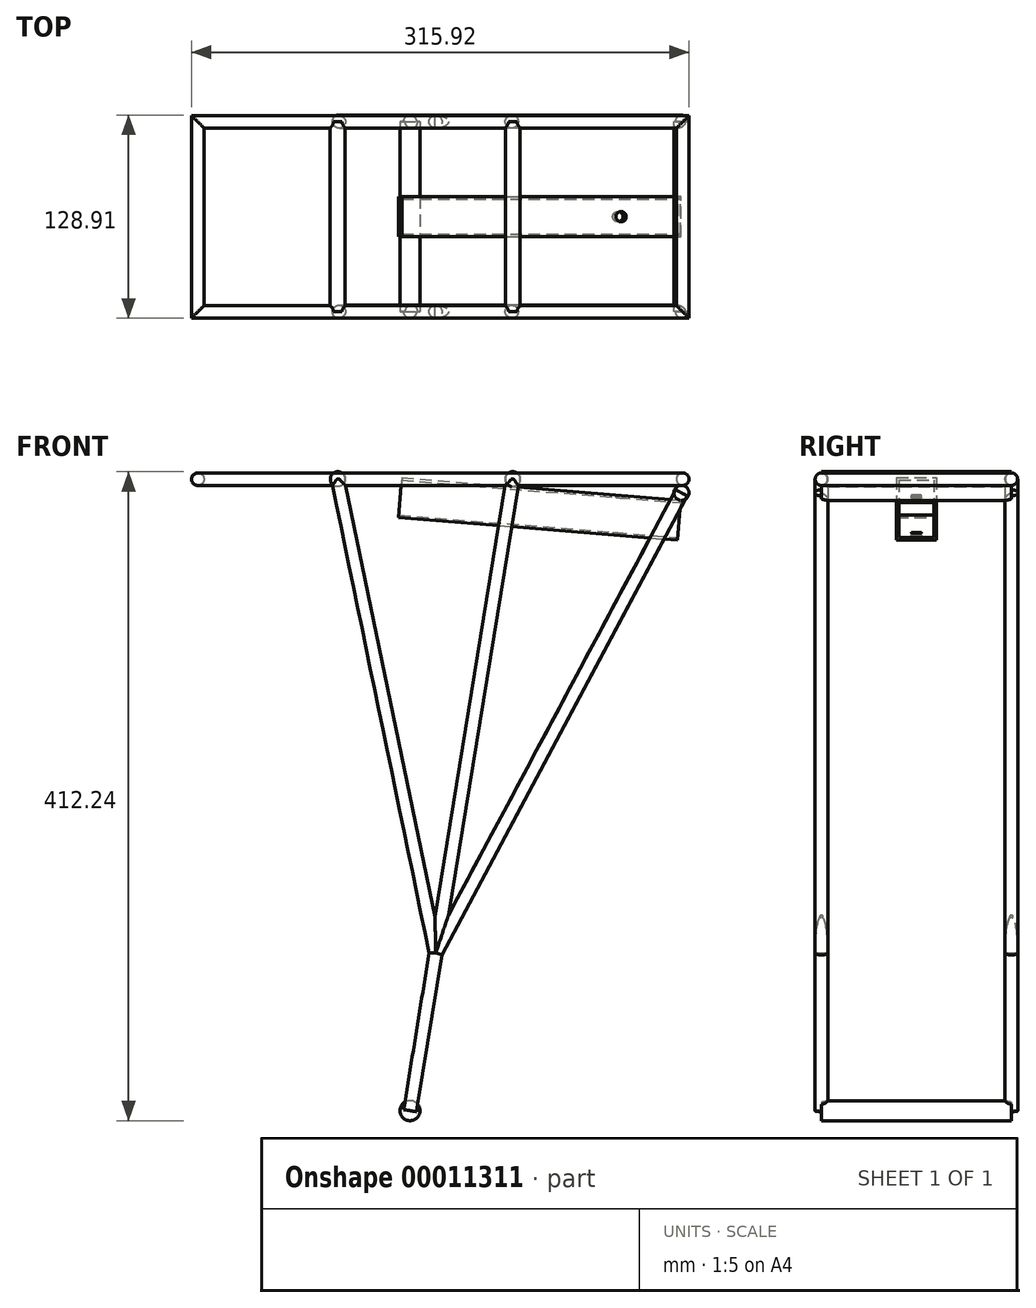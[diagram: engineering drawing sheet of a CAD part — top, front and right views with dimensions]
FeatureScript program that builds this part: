
annotation { "Feature Type Name" : "Feature", "Feature Type Description" : "" }
export const myFeature = defineFeature(function(context is Context, id is Id, definition is map)
    precondition{}
    {
        {
            var Q0;
            Q0=qCreatedBy(makeId("Top.planeOp"),FACE);
            var sketch = newSketch(context, id + "F0", { "sketchPlane" : qUnion([Q0])});
            skLineSegment(sketch, "E0.bottom", {"start": v(0, 0) * mm, "end": v(307.98, 0) * mm});
            skLineSegment(sketch, "E0.top", {"start": v(0, 120.65) * mm, "end": v(307.98, 120.65) * mm});
            skLineSegment(sketch, "E0.left", {"start": v(0, 0) * mm, "end": v(0, 120.65) * mm});
            skLineSegment(sketch, "E0.right", {"start": v(307.98, 0) * mm, "end": v(307.98, 120.65) * mm});
            skLineSegment(sketch, "E1", {"start": v(88.9, 120.65) * mm, "end": v(88.9, 0) * mm});
            skLineSegment(sketch, "E2", {"start": v(200.03, 120.65) * mm, "end": v(200.03, 0) * mm});
            skSolve(sketch);
        }
        {
            var Q0;
            Q0=qCreatedBy(makeId("Front.planeOp"),FACE);
            var sketch = newSketch(context, id + "F1", { "sketchPlane" : qUnion([Q0])});
            skCircle(sketch, "E3", {"center": v(0, 0) * mm, "radius": 3.97 * mm});
            skPoint(sketch, "E4.0", {"position": v(88.9, 0) * mm});
            skPoint(sketch, "E5.0", {"position": v(200.03, 0) * mm});
            skCircle(sketch, "E6", {"center": v(88.9, 0) * mm, "radius": 4.76 * mm});
            skCircle(sketch, "E7", {"center": v(200.03, 0) * mm, "radius": 4.76 * mm});
            skSolve(sketch);
        }
        {
            var Q0;
            Q0=makeQuery(id+"F1.imprint","IMPRINT",FACE,{"disambiguationData":[TD([[makeQuery(id+"F1.imprint","IMPRINT",EDGE,{"derivedFrom":sQuery(id+"F1.wireOp",EDGE,"E3")}),1.0]])]});
            var Q1;
            Q1=sQuery(id+"F0.wireOp",EDGE,"E0.left");
            var Q2;
            Q2=sQuery(id+"F0.wireOp",EDGE,"E0.top");
            var Q3;
            Q3=sQuery(id+"F0.wireOp",EDGE,"E0.right");
            var Q4;
            Q4=sQuery(id+"F0.wireOp",EDGE,"E0.bottom");
            sweep(context, id + "F2", {"profiles" : qUnion([Q0]), "path" : qUnion([Q1, Q2, Q3, Q4])});
        }
        {
            var Q0;
            Q0 = qSketchRegion(id + "F1", true);
            var Q1;
            Q1=sQuery(id+"F1.wireOp",EDGE,"E6");
            var Q2;
            Q2=sQuery(id+"F0.wireOp",EDGE,"E1");
            sweep(context, id + "F3", {"operationType" : NewBodyOperationType.ADD, "profiles" : qUnion([Q0]), "surfaceProfiles" : qUnion([Q1]), "path" : qUnion([Q2])});
        }
        {
            var Q0;
            Q0=qCreatedBy(makeId("Front.planeOp"),FACE);
            var sketch = newSketch(context, id + "F4", { "sketchPlane" : qUnion([Q0])});
            skCircle(sketch, "E8.0", {"center": v(307.98, 0) * mm, "radius": 3.97 * mm});
            skLineSegment(sketch, "E9", {"start": v(311.94, 0) * mm, "end": v(311.94, -8.7) * mm, "construction": true});
            skCircle(sketch, "E10", {"center": v(307.18, -8.7) * mm, "radius": 4.76 * mm});
            skCircle(sketch, "E11.0", {"center": v(200.03, 0) * mm, "radius": 4.76 * mm});
            skLineSegment(sketch, "E12", {"start": v(179.28, -3.1) * mm, "end": v(313.17, -13.96) * mm, "construction": true});
            skPoint(sketch, "E13", {"position": v(306.8, -13.44) * mm});
            skLineSegment(sketch, "E14", {"start": v(306.8, -13.44) * mm, "end": v(305.3, -31.95) * mm, "construction": true});
            skSolve(sketch);
        }
        {
            var Q0;
            Q0=qCreatedBy(makeId("Right.planeOp"),FACE);
            var Q1;
            Q1=sQuery(id+"F4.wireOp",VERTEX,"E10.center");
            cPlane(context, id + "F5", {"entities" : qUnion([Q0, Q1]), "cplaneType" : CPlaneType.PLANE_POINT, "offset" : 152.4 * mm, "width" : 152.4 * mm, "height" : 152.4 * mm});
        }
        {
            var Q0;
            Q0=qCreatedBy(id+"F5.planeOp",FACE);
            var sketch = newSketch(context, id + "F6", { "sketchPlane" : qUnion([Q0])});
            skPoint(sketch, "E15.0", {"position": v(0, -8.7) * mm});
            skCircle(sketch, "E16.0", {"center": v(120.65, 0) * mm, "radius": 3.97 * mm});
            skLineSegment(sketch, "E17", {"start": v(120.65, 0) * mm, "end": v(120.65, -21.05) * mm, "construction": true});
            skLineSegment(sketch, "E18", {"start": v(0, -8.7) * mm, "end": v(120.65, -8.7) * mm});
            skSolve(sketch);
        }
        {
            var Q0;
            Q0=makeQuery(id+"F4.imprint","IMPRINT",FACE,{"disambiguationData":[TD([[makeQuery(id+"F4.imprint","IMPRINT",EDGE,{"derivedFrom":sQuery(id+"F4.wireOp",EDGE,"E10")}),1.0]])]});
            var Q1;
            Q1=sQuery(id+"F6.wireOp",EDGE,"E18");
            sweep(context, id + "F7", {"profiles" : qUnion([Q0]), "path" : qUnion([Q1])});
        }
        {
            var Q0;
            Q0=makeQuery(id+"F7.opSweep","CAP_FACE",FACE,{"disambiguationData":[OSD([sQuery(id+"F4.wireOp",EDGE,"E10"),sQuery(id+"F6.wireOp",VERTEX,"E18.end")])],"isStart":false});
            var sketch = newSketch(context, id + "F8", { "sketchPlane" : qUnion([Q0])});
            skLineSegment(sketch, "E19.0", {"start": v(-179.28, -3.1) * mm, "end": v(-313.17, -13.96) * mm, "construction": true});
            skPoint(sketch, "E20.0", {"position": v(-306.8, -13.44) * mm});
            skLineSegment(sketch, "E21.0", {"start": v(-306.8, -13.44) * mm, "end": v(-305.3, -31.95) * mm, "construction": true});
            skCircle(sketch, "E22.0", {"center": v(-200.03, 0) * mm, "radius": 4.76 * mm, "construction": true});
            skCircle(sketch, "E23.0", {"center": v(-307.18, -8.7) * mm, "radius": 4.76 * mm, "construction": true});
            skSolve(sketch);
        }
        {
            var Q0;
            Q0=sQuery(id+"F4.wireOp",VERTEX,"E13");
            var Q1;
            Q1=sQuery(id+"F4.wireOp",VERTEX,"E14.end");
            var Q2;
            Q2=sQuery(id+"F8.wireOp",VERTEX,"E20.0");
            cPlane(context, id + "F9", {"entities" : qUnion([Q0, Q1, Q2]), "cplaneType" : CPlaneType.THREE_POINT, "offset" : 152.4 * mm, "width" : 152.4 * mm, "height" : 152.4 * mm});
        }
        {
            var Q0;
            Q0=qCreatedBy(id+"F9.planeOp",FACE);
            var sketch = newSketch(context, id + "F10", { "sketchPlane" : qUnion([Q0])});
            skLineSegment(sketch, "E24", {"start": v(0, 11.42) * mm, "end": v(-120.65, 11.42) * mm, "construction": true});
            skPoint(sketch, "E25", {"position": v(-60.33, 11.42) * mm});
            skLineSegment(sketch, "E26.bottom", {"start": v(-47.62, 11.42) * mm, "end": v(-73.03, 11.42) * mm});
            skLineSegment(sketch, "E26.top", {"start": v(-47.62, -13.98) * mm, "end": v(-73.03, -13.98) * mm});
            skLineSegment(sketch, "E26.left", {"start": v(-47.62, 11.42) * mm, "end": v(-47.62, -13.98) * mm});
            skLineSegment(sketch, "E26.right", {"start": v(-73.03, 11.42) * mm, "end": v(-73.03, -13.98) * mm});
            skSolve(sketch);
        }
        {
            var Q0;
            Q0=makeQuery(id+"F10.imprint","IMPRINT",FACE,{"disambiguationData":[TD([[makeQuery(id+"F10.imprint","IMPRINT",EDGE,{"derivedFrom":sQuery(id+"F10.wireOp",EDGE,"E26.bottom")}),1.0]])]});
            extrude(context, id + "F11", {"entities" : qUnion([Q0]), "depth" : 177.8 * mm});
        }
        {
            var Q0;
            Q0=makeQuery(id+"F11.opExtrude","CAP_FACE",FACE,{"disambiguationData":[OSD([sQuery(id+"F10.wireOp",EDGE,"E26.bottom"),sQuery(id+"F10.wireOp",EDGE,"E26.top"),sQuery(id+"F10.wireOp",EDGE,"E26.left"),sQuery(id+"F10.wireOp",EDGE,"E26.right")])],"isStart":true});
            var Q1;
            Q1=makeQuery(id+"F11.opExtrude","CAP_FACE",FACE,{"disambiguationData":[OSD([sQuery(id+"F10.wireOp",EDGE,"E26.bottom"),sQuery(id+"F10.wireOp",EDGE,"E26.top"),sQuery(id+"F10.wireOp",EDGE,"E26.left"),sQuery(id+"F10.wireOp",EDGE,"E26.right")])],"isStart":false});
            shell(context, id + "F12", {"entities" : qUnion([Q0, Q1]), "thickness" : 1.59 * mm});
        }
        {
            var Q0;
            Q0=makeQuery(id+"F11.opExtrude","SWEPT_FACE",FACE,{"disambiguationData":[OSD([sQuery(id+"F10.wireOp",EDGE,"E26.bottom")])]});
            var sketch = newSketch(context, id + "F13", { "sketchPlane" : qUnion([Q0])});
            skLineSegment(sketch, "E27.0.0", {"start": v(306.88, 47.62) * mm, "end": v(306.88, 73.03) * mm, "construction": true});
            skLineSegment(sketch, "E27.0.1", {"start": v(306.88, 73.03) * mm, "end": v(129.08, 73.03) * mm, "construction": true});
            skLineSegment(sketch, "E27.0.2", {"start": v(129.08, 73.03) * mm, "end": v(129.08, 47.62) * mm, "construction": true});
            skLineSegment(sketch, "E27.0.3", {"start": v(129.08, 47.62) * mm, "end": v(306.88, 47.62) * mm, "construction": true});
            skLineSegment(sketch, "E28", {"start": v(129.08, 60.33) * mm, "end": v(306.88, 60.33) * mm, "construction": true});
            skCircle(sketch, "E29", {"center": v(268.78, 60.32) * mm, "radius": 3.26 * mm});
            skSolve(sketch);
        }
        {
            var Q0;
            Q0=makeQuery(id+"F13.imprint","IMPRINT",FACE,{"disambiguationData":[TD([[makeQuery(id+"F13.imprint","IMPRINT",EDGE,{"derivedFrom":sQuery(id+"F13.wireOp",EDGE,"E29")}),1.0]])]});
            var Q1;
            Q1=makeQuery(id+"F11.opExtrude","SWEPT_FACE",FACE,{"disambiguationData":[OSD([sQuery(id+"F10.wireOp",EDGE,"E26.top")])]});
            extrude(context, id + "F14", {"entities" : qUnion([Q0]), "operationType" : NewBodyOperationType.REMOVE, "endBound" : BoundingType.UP_TO_SURFACE, "oppositeDirection" : true, "endBoundEntityFace" : qUnion([Q1]), "depth" : 25.4 * mm});
        }
        {
            var Q0;
            Q0=qCreatedBy(makeId("Front.planeOp"),FACE);
            var sketch = newSketch(context, id + "F15", { "sketchPlane" : qUnion([Q0])});
            skCircle(sketch, "E30.0", {"center": v(200.03, 0) * mm, "radius": 4.76 * mm});
            skCircle(sketch, "E31.0", {"center": v(307.18, -8.7) * mm, "radius": 4.76 * mm});
            skLineSegment(sketch, "E32", {"start": v(200.03, 0) * mm, "end": v(134.81, -401.13) * mm});
            skLineSegment(sketch, "E33", {"start": v(134.81, -401.13) * mm, "end": v(307.18, -8.7) * mm});
            skCircle(sketch, "E34", {"center": v(134.81, -401.13) * mm, "radius": 6.35 * mm});
            skSolve(sketch);
        }
        {
            var Q0;
            {var subQ1=sQuery(id+"F15.wireOp",EDGE,"E33");var subQ3=sQuery(id+"F15.wireOp",EDGE,"E32");var subQ5=makeQuery(id+"F15.imprint","INTERSECT",VERTEX,{"derivedFrom":[subQ3,subQ1]});Q0=makeQuery(id+"F15.imprint","IMPRINT",FACE,{"disambiguationData":[TD([[makeQuery(id+"F15.imprint","IMPRINT",EDGE,{"disambiguationData":[TD([[subQ5,1.0]])],"derivedFrom":subQ3}),-1.0]])]});}
            var Q1;
            {var subQ1=sQuery(id+"F15.wireOp",EDGE,"E33");var subQ3=sQuery(id+"F15.wireOp",EDGE,"E32");var subQ5=makeQuery(id+"F15.imprint","INTERSECT",VERTEX,{"derivedFrom":[subQ3,subQ1]});Q1=makeQuery(id+"F15.imprint","IMPRINT",FACE,{"disambiguationData":[TD([[makeQuery(id+"F15.imprint","IMPRINT",EDGE,{"disambiguationData":[TD([[subQ5,1.0]])],"derivedFrom":subQ3}),1.0]])]});}
            extrude(context, id + "F16", {"entities" : qUnion([Q0, Q1]), "oppositeDirection" : true, "depth" : 120.65 * mm});
        }
        {
            var Q0;
            Q0=qCreatedBy(makeId("Front.planeOp"),FACE);
            var sketch = newSketch(context, id + "F17", { "sketchPlane" : qUnion([Q0])});
            skPoint(sketch, "E35.0", {"position": v(0, 0) * mm});
            skPoint(sketch, "E36.0", {"position": v(88.9, 0) * mm});
            skPoint(sketch, "E37.0", {"position": v(200.03, 0) * mm});
            skPoint(sketch, "E38.0", {"position": v(307.18, -8.7) * mm});
            skCircle(sketch, "E39.0", {"center": v(134.81, -401.13) * mm, "radius": 6.35 * mm});
            skLineSegment(sketch, "E40", {"start": v(200.03, 0) * mm, "end": v(134.81, -401.13) * mm});
            skPoint(sketch, "E41", {"position": v(151.11, -300.85) * mm});
            skLineSegment(sketch, "E42", {"start": v(88.9, 0) * mm, "end": v(151.11, -300.85) * mm});
            skLineSegment(sketch, "E43", {"start": v(307.18, -8.7) * mm, "end": v(151.11, -300.85) * mm});
            skSolve(sketch);
        }
        {
            var Q0;
            Q0=sQuery(id+"F17.wireOp",EDGE,"E40");
            var Q1;
            Q1=sQuery(id+"F17.wireOp",VERTEX,"E37.0");
            cPlane(context, id + "F18", {"entities" : qUnion([Q0, Q1]), "cplaneType" : CPlaneType.LINE_POINT, "offset" : 152.4 * mm, "width" : 152.4 * mm, "height" : 152.4 * mm});
        }
        {
            var Q0;
            Q0=qCreatedBy(id+"F18.planeOp",FACE);
            var sketch = newSketch(context, id + "F19", { "sketchPlane" : qUnion([Q0])});
            skPoint(sketch, "E44.0", {"position": v(197.43, 0) * mm});
            skCircle(sketch, "E45", {"center": v(197.43, 0) * mm, "radius": 4.13 * mm});
            skPoint(sketch, "E46.0", {"position": v(197.43, -120.65) * mm});
            skCircle(sketch, "E47", {"center": v(197.43, -120.65) * mm, "radius": 4.13 * mm});
            skSolve(sketch);
        }
        {
            var Q0;
            Q0 = qSketchRegion(id + "F19", true);
            var Q1;
            Q1=sQuery(id+"F17.wireOp",EDGE,"E40");
            sweep(context, id + "F20", {"operationType" : NewBodyOperationType.ADD, "profiles" : qUnion([Q0]), "path" : qUnion([Q1])});
        }
        {
            var Q0;
            Q0=sQuery(id+"F17.wireOp",EDGE,"E42");
            var Q1;
            Q1=sQuery(id+"F17.wireOp",VERTEX,"E36.0");
            cPlane(context, id + "F21", {"entities" : qUnion([Q0, Q1]), "cplaneType" : CPlaneType.LINE_POINT, "offset" : 152.4 * mm, "width" : 152.4 * mm, "height" : 152.4 * mm});
        }
        {
            var Q0;
            Q0=qCreatedBy(id+"F21.planeOp",FACE);
            var sketch = newSketch(context, id + "F22", { "sketchPlane" : qUnion([Q0])});
            skPoint(sketch, "E48.0", {"position": v(87.06, 0) * mm});
            skCircle(sketch, "E49", {"center": v(87.06, 0) * mm, "radius": 4.13 * mm});
            skPoint(sketch, "E50.0", {"position": v(87.06, -120.65) * mm});
            skCircle(sketch, "E51", {"center": v(87.06, -120.65) * mm, "radius": 4.13 * mm});
            skSolve(sketch);
        }
        {
            var Q0;
            Q0 = qSketchRegion(id + "F22", true);
            var Q1;
            Q1=sQuery(id+"F17.wireOp",EDGE,"E42");
            sweep(context, id + "F23", {"operationType" : NewBodyOperationType.ADD, "profiles" : qUnion([Q0]), "path" : qUnion([Q1])});
        }
        {
            var Q0;
            Q0=sQuery(id+"F17.wireOp",EDGE,"E43");
            var Q1;
            Q1=sQuery(id+"F17.wireOp",VERTEX,"E38.0");
            cPlane(context, id + "F24", {"entities" : qUnion([Q0, Q1]), "cplaneType" : CPlaneType.LINE_POINT, "offset" : 152.4 * mm, "width" : 152.4 * mm, "height" : 152.4 * mm});
        }
        {
            var Q0;
            Q0=qCreatedBy(id+"F24.planeOp",FACE);
            var sketch = newSketch(context, id + "F25", { "sketchPlane" : qUnion([Q0])});
            skPoint(sketch, "E52.0", {"position": v(275.04, 0) * mm});
            skCircle(sketch, "E53", {"center": v(275.04, 0) * mm, "radius": 4.13 * mm});
            skPoint(sketch, "E54.0", {"position": v(275.04, -120.65) * mm});
            skCircle(sketch, "E55", {"center": v(275.04, -120.65) * mm, "radius": 4.13 * mm});
            skSolve(sketch);
        }
        {
            var Q0;
            Q0 = qSketchRegion(id + "F25", true);
            var Q1;
            Q1=sQuery(id+"F17.wireOp",EDGE,"E43");
            sweep(context, id + "F26", {"operationType" : NewBodyOperationType.ADD, "profiles" : qUnion([Q0]), "path" : qUnion([Q1])});
        }
        {
            var Q0;
            Q0=qCreatedBy(makeId("Front.planeOp"),FACE);
            var Q1;
            Q1=sQuery(id+"F6.wireOp",VERTEX,"E17.start");
            cPlane(context, id + "F27", {"entities" : qUnion([Q0, Q1]), "cplaneType" : CPlaneType.PLANE_POINT, "offset" : 152.4 * mm, "width" : 152.4 * mm, "height" : 152.4 * mm});
        }
    });
